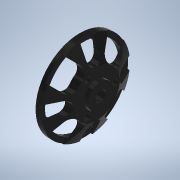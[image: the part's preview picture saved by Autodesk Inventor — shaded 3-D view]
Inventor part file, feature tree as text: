
AUTODESK INVENTOR PART (.ipt)
format: ipt  version: 2022 (Build 260153000, 153)  size: 361,984 bytes
history: native  units: in
note: dims shown in document units (in); Inventor stores cm internally (conversion verified against a paired STEP export)
features: fillet x2, sketch x2, revolve x1, extrude x1
ambient origin geometry x8: Origin, YZ Plane, XZ Plane, XY Plane, X Axis, Y Axis, Z Axis, Center Point
bodies: Solid1 (feature_tree)
feature tree (6):
  revolve  "Revolution1"  [1 undecoded]
  extrude  "Extrusion1"  Depth=0.0197in
  fillet  "Fillet1"  Radius=0.0787in
  fillet  "Fillet2"  Radius=0.2362in
  sketch  "Sketch1"  dims[d0=0.1181in d1=0.8268in]
  sketch  "Sketch2"  dims[d2=0.315in d3=0.4331in d4=0.0787in d5=0.2362in d6=0.0984in d7=360.0deg d8=0.1575in d9=0.0984in d10=0.0295in d11=0.2953in d12=0.1378in d13=0.2165in d15=0.1476in d16=0.2461in d18=45.0deg d19=0.4331in d20=0.5118in d21=0.8661in d22=1.5748in d24=360.0deg d26=0.2362in d27=0.0in d28=0.125in d29=0.0197in d30=0.5906in d31=0.1181in d32=1.1811in d34=360.0deg]
note: 1 required parameter value undecoded (feature->parameter linkage not recoverable at this tier; creation-order binding heuristic only, values carry confidence <= 0.55)
